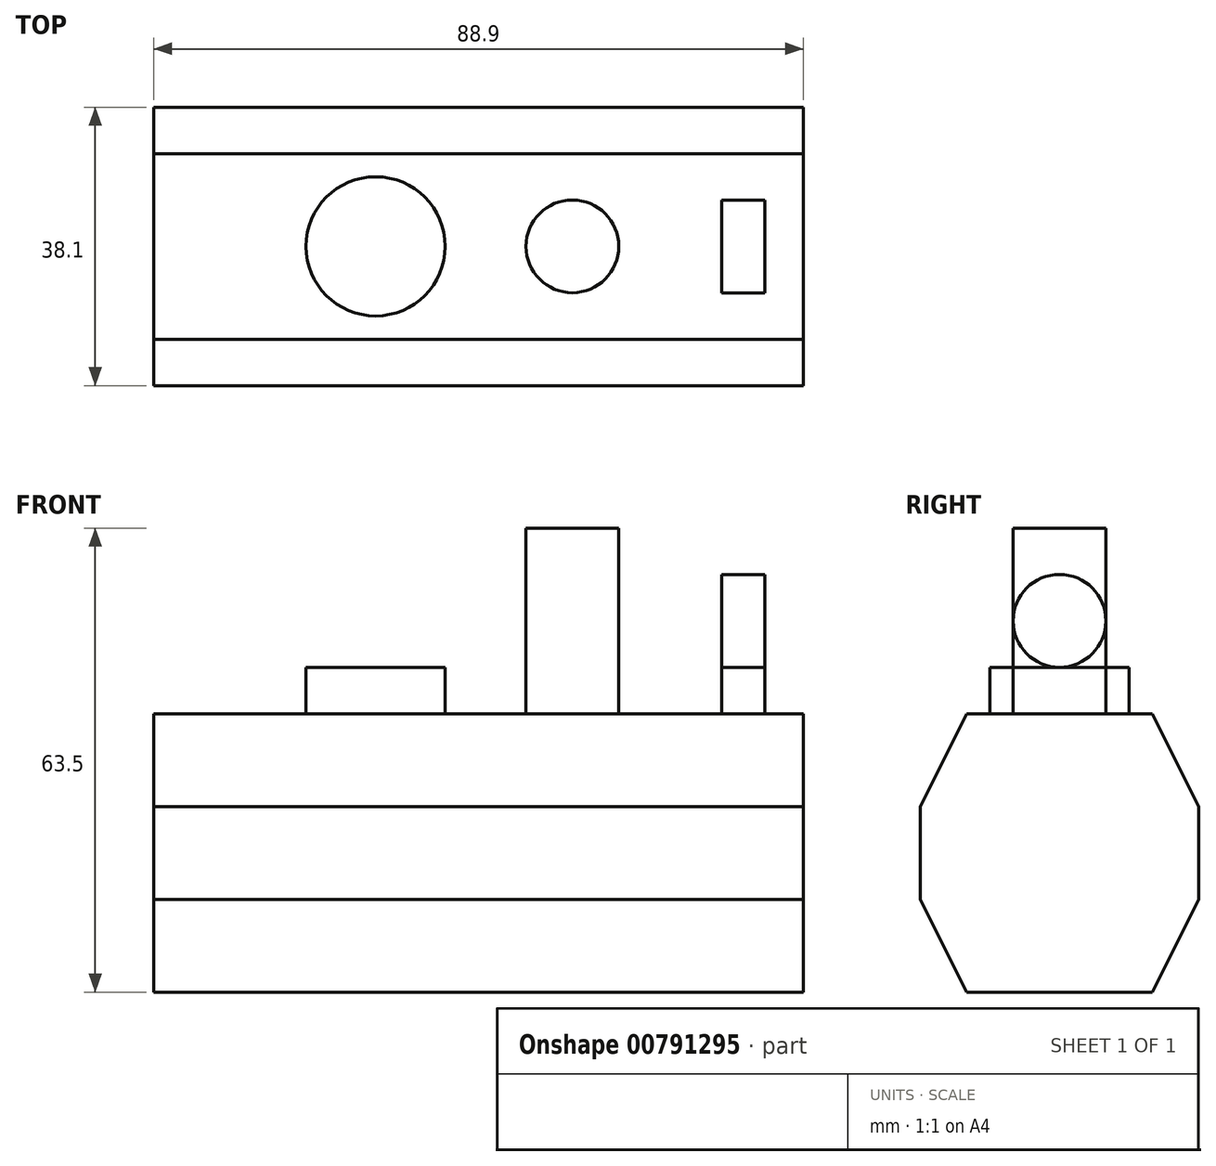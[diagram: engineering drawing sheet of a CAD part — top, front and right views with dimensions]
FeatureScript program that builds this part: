
annotation { "Feature Type Name" : "Feature", "Feature Type Description" : "" }
export const myFeature = defineFeature(function(context is Context, id is Id, definition is map)
    precondition{}
    {
        {
            var Q0;
            Q0=qCreatedBy(makeId("Front.planeOp"),FACE);
            var sketch = newSketch(context, id + "F0", { "sketchPlane" : qUnion([Q0])});
            skLineSegment(sketch, "E0.bottom", {"start": v(-41.2, 31.8) * mm, "end": v(47.7, 31.8) * mm});
            skLineSegment(sketch, "E0.top", {"start": v(-41.2, -6.3) * mm, "end": v(47.7, -6.3) * mm});
            skLineSegment(sketch, "E0.left", {"start": v(-41.2, 31.8) * mm, "end": v(-41.2, -6.3) * mm});
            skLineSegment(sketch, "E0.right", {"start": v(47.7, 31.8) * mm, "end": v(47.7, -6.3) * mm});
            skSolve(sketch);
        }
        {
            var Q0;
            Q0=qSketchRegion(id+"F0",true);
            extrude(context, id + "F1", {"entities" : qUnion([Q0]), "depth" : 38.1 * mm});
        }
        {
            var Q0;
            Q0=makeQuery(id+"F1.opExtrude","SWEPT_FACE",FACE,{"disambiguationData":[OSD([sQuery(id+"F0.wireOp",EDGE,"E0.left")])]});
            var sketch = newSketch(context, id + "F2", { "sketchPlane" : qUnion([Q0])});
            skLineSegment(sketch, "E1", {"start": v(0, 19.1) * mm, "end": v(6.35, 31.8) * mm});
            skLineSegment(sketch, "E2", {"start": v(31.75, 31.8) * mm, "end": v(38.1, 19.1) * mm});
            skLineSegment(sketch, "E3", {"start": v(0, 6.4) * mm, "end": v(6.35, -6.3) * mm});
            skLineSegment(sketch, "E4", {"start": v(38.1, 6.4) * mm, "end": v(31.75, -6.3) * mm});
            skSolve(sketch);
        }
        {
            var Q0;
            {var subQ0=sQuery(id+"F2.wireOp",EDGE,"E1");Q0=makeQuery(id+"F2.imprint","IMPRINT",FACE,{"disambiguationData":[TD([[makeQuery(id+"F2.imprint","IMPRINT",EDGE,{"derivedFrom":subQ0}),1.0]])]});}
            var Q1;
            {var subQ0=sQuery(id+"F2.wireOp",EDGE,"E3");Q1=makeQuery(id+"F2.imprint","IMPRINT",FACE,{"disambiguationData":[TD([[makeQuery(id+"F2.imprint","IMPRINT",EDGE,{"derivedFrom":subQ0}),-1.0]])]});}
            var Q2;
            {var subQ0=sQuery(id+"F2.wireOp",EDGE,"E4");Q2=makeQuery(id+"F2.imprint","IMPRINT",FACE,{"disambiguationData":[TD([[makeQuery(id+"F2.imprint","IMPRINT",EDGE,{"derivedFrom":subQ0}),1.0]])]});}
            var Q3;
            {var subQ0=sQuery(id+"F2.wireOp",EDGE,"E2");Q3=makeQuery(id+"F2.imprint","IMPRINT",FACE,{"disambiguationData":[TD([[makeQuery(id+"F2.imprint","IMPRINT",EDGE,{"derivedFrom":subQ0}),1.0]])]});}
            extrude(context, id + "F3", {"entities" : qUnion([Q0, Q1, Q2, Q3]), "operationType" : NewBodyOperationType.REMOVE, "endBound" : BoundingType.THROUGH_ALL, "oppositeDirection" : true, "depth" : 25.4 * mm});
        }
        {
            var Q0;
            Q0=makeQuery(id+"F1.opExtrude","SWEPT_FACE",FACE,{"disambiguationData":[OSD([sQuery(id+"F0.wireOp",EDGE,"E0.bottom")])]});
            var sketch = newSketch(context, id + "F4", { "sketchPlane" : qUnion([Q0])});
            skCircle(sketch, "E5", {"center": v(16.1, -19.05) * mm, "radius": 6.35 * mm});
            skCircle(sketch, "E6", {"center": v(-10.83, -19.05) * mm, "radius": 9.53 * mm});
            skLineSegment(sketch, "E7.bottom", {"start": v(36.52, -12.7) * mm, "end": v(42.4, -12.7) * mm});
            skLineSegment(sketch, "E7.top", {"start": v(36.52, -25.4) * mm, "end": v(42.4, -25.4) * mm});
            skLineSegment(sketch, "E7.left", {"start": v(36.52, -12.7) * mm, "end": v(36.52, -25.4) * mm});
            skLineSegment(sketch, "E7.right", {"start": v(42.4, -12.7) * mm, "end": v(42.4, -25.4) * mm});
            skSolve(sketch);
        }
        {
            var Q0;
            Q0=makeQuery(id+"F4.imprint","IMPRINT",FACE,{"disambiguationData":[TD([[makeQuery(id+"F4.imprint","IMPRINT",EDGE,{"derivedFrom":sQuery(id+"F4.wireOp",EDGE,"E5")}),1.0]])]});
            extrude(context, id + "F5", {"entities" : qUnion([Q0]), "operationType" : NewBodyOperationType.ADD, "depth" : 25.4 * mm});
        }
        {
            var Q0;
            Q0=makeQuery(id+"F4.imprint","IMPRINT",FACE,{"disambiguationData":[TD([[makeQuery(id+"F4.imprint","IMPRINT",EDGE,{"derivedFrom":sQuery(id+"F4.wireOp",EDGE,"E6")}),1.0]])]});
            extrude(context, id + "F6", {"entities" : qUnion([Q0]), "operationType" : NewBodyOperationType.ADD, "depth" : 6.35 * mm});
        }
        {
            var Q0;
            Q0=makeQuery(id+"F4.imprint","IMPRINT",FACE,{"disambiguationData":[TD([[makeQuery(id+"F4.imprint","IMPRINT",EDGE,{"derivedFrom":sQuery(id+"F4.wireOp",EDGE,"E7.bottom")}),-1.0]])]});
            extrude(context, id + "F7", {"entities" : qUnion([Q0]), "operationType" : NewBodyOperationType.ADD, "depth" : 19.05 * mm});
        }
        {
            var Q0;
            Q0=makeQuery(id+"F7.opExtrude","SWEPT_FACE",FACE,{"disambiguationData":[OSD([sQuery(id+"F4.wireOp",EDGE,"E7.right")])]});
            var sketch = newSketch(context, id + "F8", { "sketchPlane" : qUnion([Q0])});
            skLineSegment(sketch, "E8", {"start": v(-25.4, 38.15) * mm, "end": v(-12.7, 38.15) * mm});
            skCircle(sketch, "E9", {"center": v(-19.05, 44.5) * mm, "radius": 6.35 * mm});
            skPoint(sketch, "E9.centerSnap0", {"position": v(-19.05, 50.85) * mm});
            skSolve(sketch);
        }
        {
            var Q0;
            {var subQ0=sQuery(id+"F8.wireOp",EDGE,"E9");var subQ1=sQuery(id+"F4.wireOp",EDGE,"E7.right");var subQ2=makeQuery(id+"F7.opExtrude","CAP_EDGE",EDGE,{"disambiguationData":[OSD([subQ1])],"isStart":false});var subQ3=makeQuery(id+"F8.imprint","INTERSECT",VERTEX,{"derivedFrom":[subQ2,subQ0]});Q0=makeQuery(id+"F8.imprint","IMPRINT",FACE,{"disambiguationData":[TD([[makeQuery(id+"F8.imprint","IMPRINT",EDGE,{"disambiguationData":[TD([[subQ3,1.0]])],"derivedFrom":subQ0}),-1.0]])]});}
            var Q1;
            {var subQ0=sQuery(id+"F8.wireOp",EDGE,"E8");var subQ3=sQuery(id+"F8.wireOp",EDGE,"E9");var subQ4=makeQuery(id+"F8.imprint","INTERSECT",VERTEX,{"derivedFrom":[subQ0,subQ3]});Q1=makeQuery(id+"F8.imprint","IMPRINT",FACE,{"disambiguationData":[TD([[makeQuery(id+"F8.imprint","IMPRINT",EDGE,{"disambiguationData":[TD([[subQ4,-1.0]])],"derivedFrom":subQ0}),1.0]])]});}
            var Q2;
            {var subQ0=sQuery(id+"F8.wireOp",EDGE,"E8");var subQ3=sQuery(id+"F8.wireOp",EDGE,"E9");var subQ4=makeQuery(id+"F8.imprint","INTERSECT",VERTEX,{"derivedFrom":[subQ0,subQ3]});Q2=makeQuery(id+"F8.imprint","IMPRINT",FACE,{"disambiguationData":[TD([[makeQuery(id+"F8.imprint","IMPRINT",EDGE,{"disambiguationData":[TD([[subQ4,1.0]])],"derivedFrom":subQ0}),1.0]])]});}
            var Q3;
            {var subQ0=sQuery(id+"F8.wireOp",EDGE,"E9");var subQ1=sQuery(id+"F4.wireOp",EDGE,"E7.right");var subQ2=makeQuery(id+"F7.opExtrude","CAP_EDGE",EDGE,{"disambiguationData":[OSD([subQ1])],"isStart":false});var subQ3=makeQuery(id+"F8.imprint","INTERSECT",VERTEX,{"derivedFrom":[subQ2,subQ0]});Q3=makeQuery(id+"F8.imprint","IMPRINT",FACE,{"disambiguationData":[TD([[makeQuery(id+"F8.imprint","IMPRINT",EDGE,{"disambiguationData":[TD([[subQ3,-1.0]])],"derivedFrom":subQ0}),-1.0]])]});}
            extrude(context, id + "F9", {"entities" : qUnion([Q0, Q1, Q2, Q3]), "operationType" : NewBodyOperationType.REMOVE, "endBound" : BoundingType.UP_TO_NEXT, "oppositeDirection" : true, "depth" : 25.4 * mm});
        }
    });
